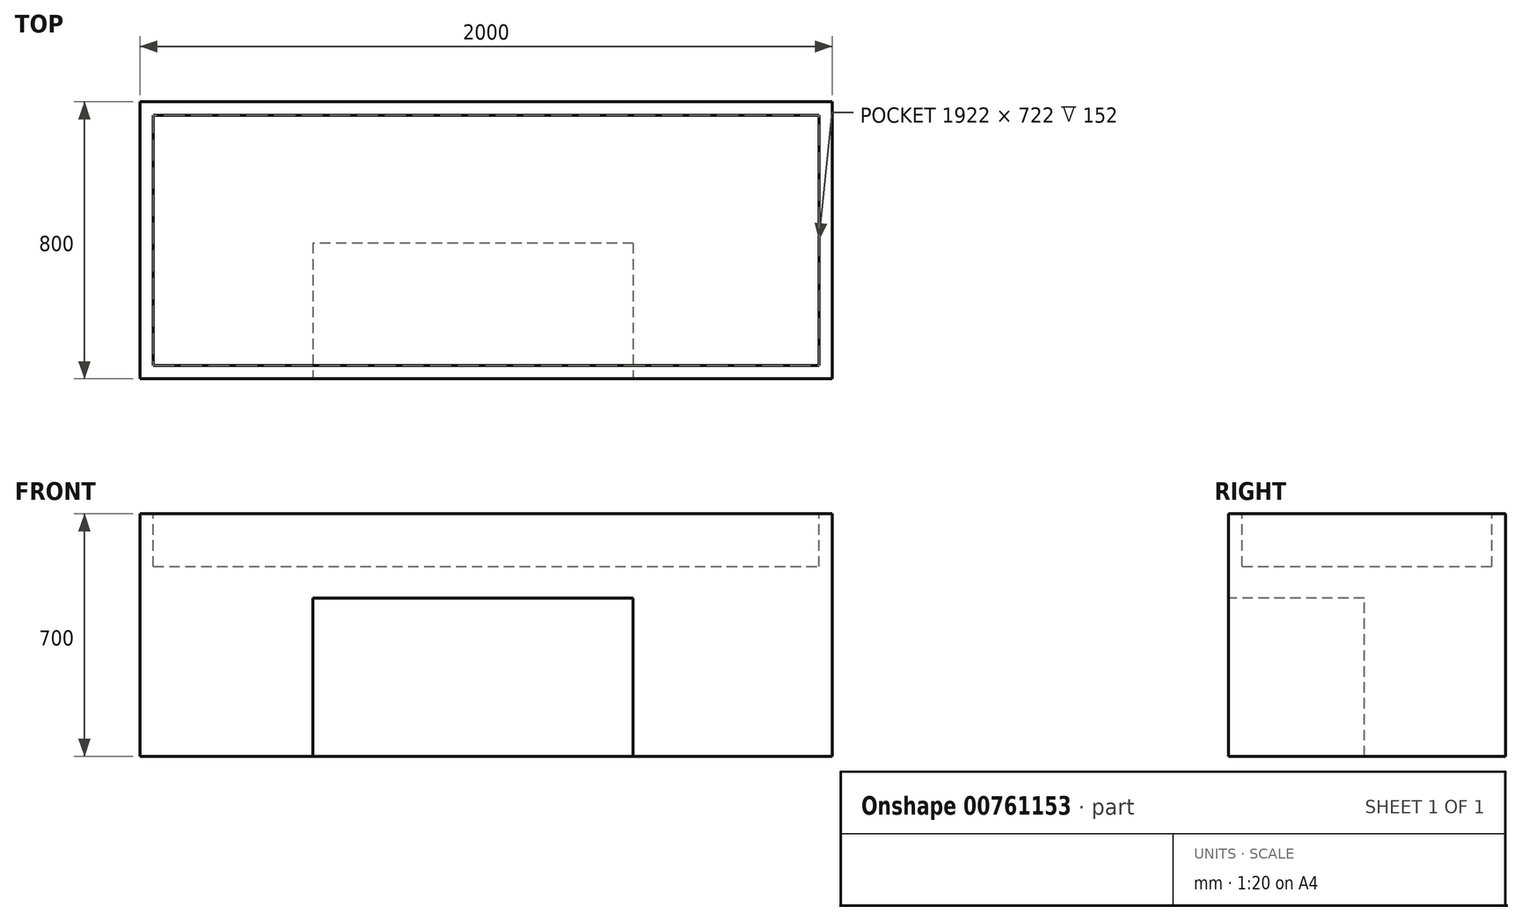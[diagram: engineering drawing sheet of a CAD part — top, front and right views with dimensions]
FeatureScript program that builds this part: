
annotation { "Feature Type Name" : "Feature", "Feature Type Description" : "" }
export const myFeature = defineFeature(function(context is Context, id is Id, definition is map)
    precondition{}
    {
        {
            var Q0;
            Q0=qCreatedBy(makeId("Top.planeOp"),FACE);
            var sketch = newSketch(context, id + "F0", { "sketchPlane" : qUnion([Q0])});
            skLineSegment(sketch, "E0.top", {"start": v(0, -250) * mm, "end": v(1500, -250) * mm});
            skLineSegment(sketch, "E0.right", {"start": v(1500, 0) * mm, "end": v(1500, -250) * mm});
            skLineSegment(sketch, "E1.bottom", {"start": v(1500, -250) * mm, "end": v(-500, -250) * mm});
            skLineSegment(sketch, "E1.top", {"start": v(1500, 550) * mm, "end": v(-500, 550) * mm});
            skLineSegment(sketch, "E1.left", {"start": v(1500, -250) * mm, "end": v(1500, 550) * mm});
            skLineSegment(sketch, "E1.right", {"start": v(-500, -250) * mm, "end": v(-500, 550) * mm});
            skSolve(sketch);
        }
        {
            var Q0;
            {var subQ4=sQuery(id+"F0.wireOp",EDGE,"E1.top");Q0=makeQuery(id+"F0.imprint","IMPRINT",FACE,{"disambiguationData":[TD([[makeQuery(id+"F0.imprint","IMPRINT",EDGE,{"derivedFrom":subQ4}),1.0]])]});}
            extrude(context, id + "F1", {"entities" : qUnion([Q0]), "depth" : 700 * mm, "offsetDistance" : 25 * mm});
        }
        {
            var Q0;
            Q0=makeQuery(id+"F1.opExtrude","SWEPT_FACE",FACE,{"disambiguationData":[OSD([sQuery(id+"F0.wireOp",EDGE,"E1.bottom")])]});
            var sketch = newSketch(context, id + "F2", { "sketchPlane" : qUnion([Q0])});
            skLineSegment(sketch, "E2.bottom", {"start": v(0, 0) * mm, "end": v(924.52, 0) * mm});
            skLineSegment(sketch, "E2.top", {"start": v(0, 457.3) * mm, "end": v(924.52, 457.3) * mm});
            skLineSegment(sketch, "E2.left", {"start": v(0, 0) * mm, "end": v(0, 457.3) * mm});
            skLineSegment(sketch, "E2.right", {"start": v(924.52, 0) * mm, "end": v(924.52, 457.3) * mm});
            skSolve(sketch);
        }
        {
            var Q0;
            Q0=makeQuery(id+"F2.imprint","IMPRINT",FACE,{"disambiguationData":[TD([[makeQuery(id+"F2.imprint","IMPRINT",EDGE,{"derivedFrom":sQuery(id+"F2.wireOp",EDGE,"E2.bottom")}),-1.0]])]});
            extrude(context, id + "F3", {"entities" : qUnion([Q0]), "operationType" : NewBodyOperationType.REMOVE, "oppositeDirection" : true, "depth" : 392 * mm, "offsetDistance" : 25 * mm});
        }
        {
            var Q0;
            Q0=makeQuery(id+"F1.opExtrude","CAP_FACE",FACE,{"disambiguationData":[OSD([sQuery(id+"F0.wireOp",EDGE,"E1.bottom"),sQuery(id+"F0.wireOp",EDGE,"E1.top"),sQuery(id+"F0.wireOp",EDGE,"E1.left"),sQuery(id+"F0.wireOp",EDGE,"E1.right")])],"isStart":false});
            var sketch = newSketch(context, id + "F4", { "sketchPlane" : qUnion([Q0])});
            skLineSegment(sketch, "E3.0", {"start": v(1461, -211) * mm, "end": v(1461, 511) * mm});
            skLineSegment(sketch, "E3.1", {"start": v(-461, -211) * mm, "end": v(1461, -211) * mm});
            skLineSegment(sketch, "E3.2", {"start": v(-461, 511) * mm, "end": v(-461, -211) * mm});
            skLineSegment(sketch, "E3.3", {"start": v(1461, 511) * mm, "end": v(-461, 511) * mm});
            skSolve(sketch);
        }
        {
            var Q0;
            Q0=makeQuery(id+"F4.imprint","IMPRINT",FACE,{"disambiguationData":[TD([[makeQuery(id+"F4.imprint","IMPRINT",EDGE,{"derivedFrom":sQuery(id+"F4.wireOp",EDGE,"E3.0")}),1.0]])]});
            extrude(context, id + "F5", {"entities" : qUnion([Q0]), "operationType" : NewBodyOperationType.REMOVE, "oppositeDirection" : true, "depth" : 152 * mm, "offsetDistance" : 25 * mm});
        }
    });
